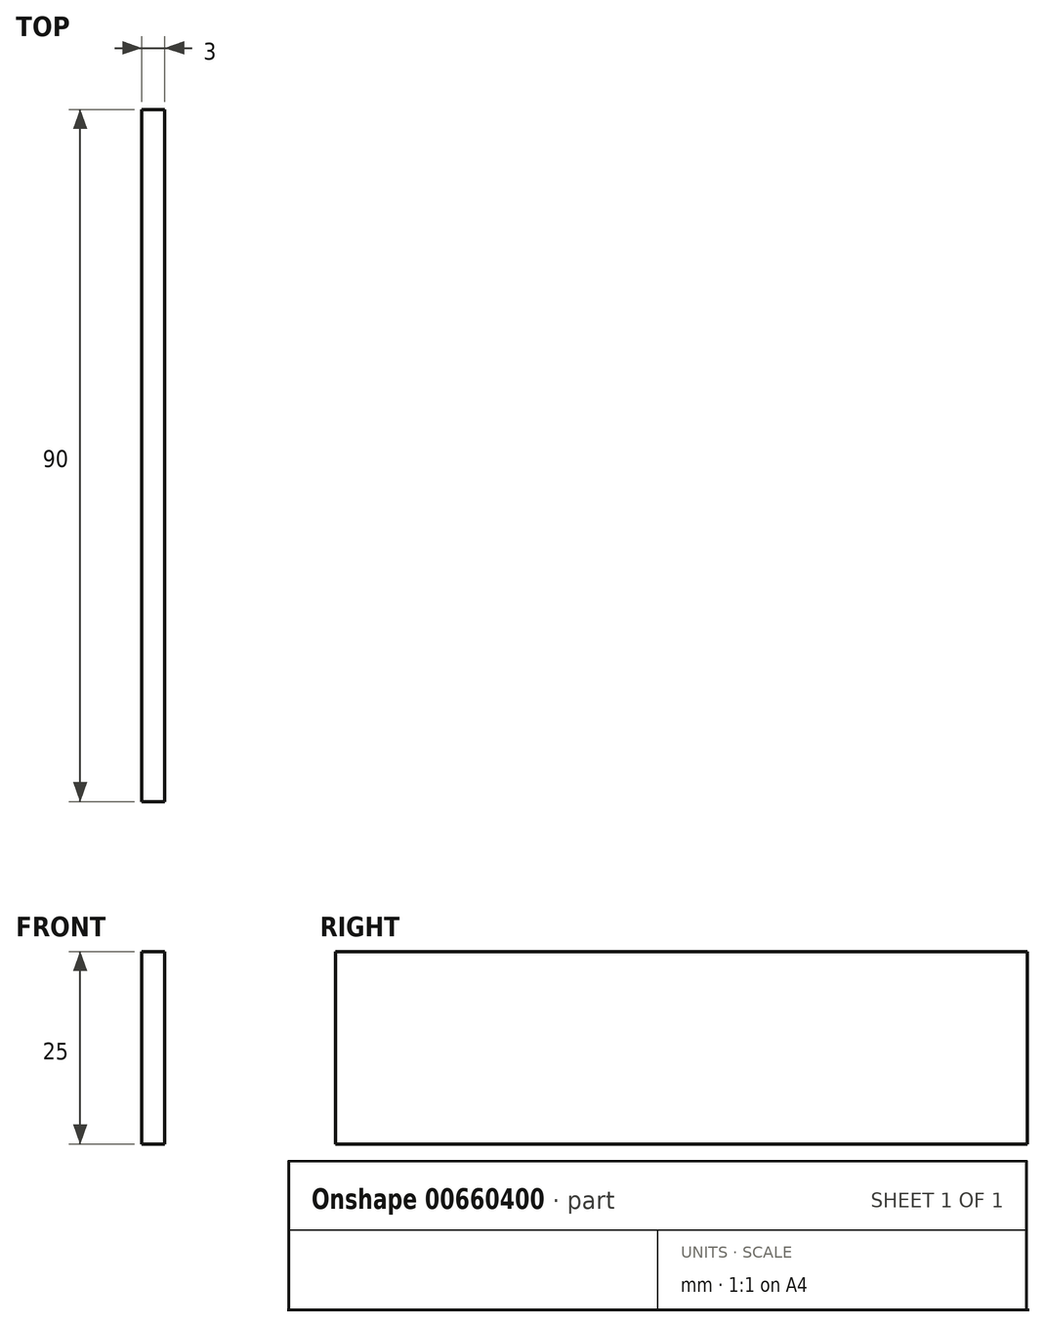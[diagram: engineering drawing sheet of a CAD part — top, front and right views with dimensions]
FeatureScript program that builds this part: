
annotation { "Feature Type Name" : "Feature", "Feature Type Description" : "" }
export const myFeature = defineFeature(function(context is Context, id is Id, definition is map)
    precondition{}
    {
        {
            var Q0;
            Q0=qCreatedBy(makeId("Front.planeOp"),FACE);
            var sketch = newSketch(context, id + "F0", { "sketchPlane" : qUnion([Q0])});
            skLineSegment(sketch, "E0.bottom", {"start": v(0, 0) * mm, "end": v(3, 0) * mm});
            skLineSegment(sketch, "E0.top", {"start": v(0, 25) * mm, "end": v(3, 25) * mm});
            skLineSegment(sketch, "E0.left", {"start": v(0, 0) * mm, "end": v(0, 25) * mm});
            skLineSegment(sketch, "E0.right", {"start": v(3, 0) * mm, "end": v(3, 25) * mm});
            skSolve(sketch);
        }
        {
            var Q0;
            Q0=makeQuery(id+"F0.imprint","IMPRINT",FACE,{"disambiguationData":[TD([[makeQuery(id+"F0.imprint","IMPRINT",EDGE,{"derivedFrom":sQuery(id+"F0.wireOp",EDGE,"E0.bottom")}),1.0]])]});
            extrude(context, id + "F1", {"entities" : qUnion([Q0]), "depth" : 90 * mm, "offsetDistance" : 25 * mm});
        }
    });
